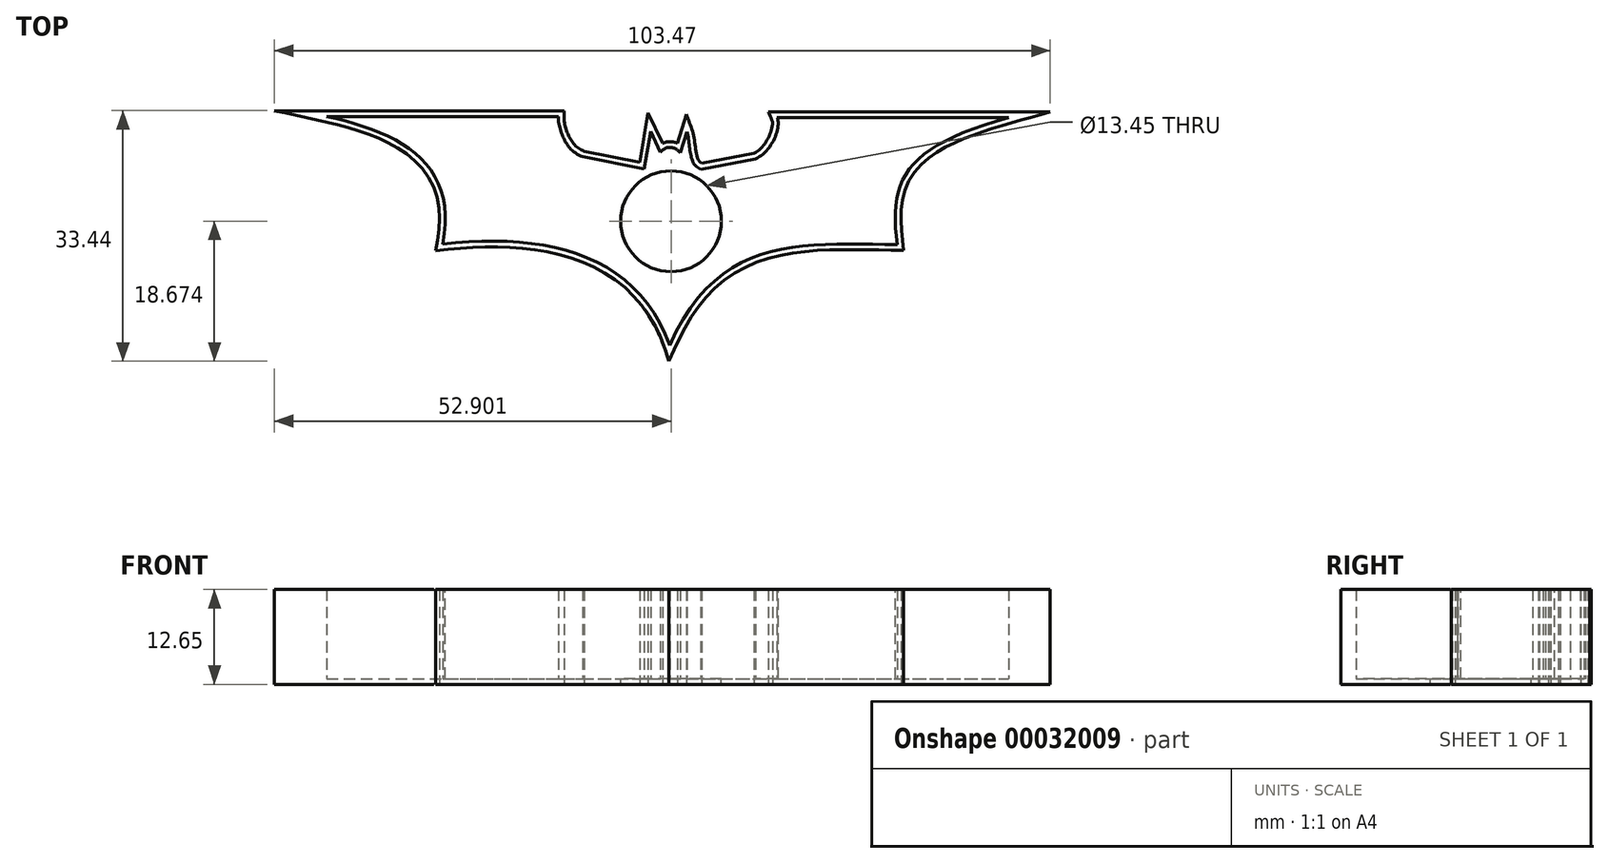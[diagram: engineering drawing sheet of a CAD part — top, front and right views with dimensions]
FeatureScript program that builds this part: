
annotation { "Feature Type Name" : "Feature", "Feature Type Description" : "" }
export const myFeature = defineFeature(function(context is Context, id is Id, definition is map)
    precondition{}
    {
        {
            var Q0;
            Q0=qCreatedBy(makeId("Top.planeOp"),FACE);
            var sketch = newSketch(context, id + "F0", { "sketchPlane" : qUnion([Q0])});
            skLineSegment(sketch, "E0", {"start": v(-52.23, 32.47) * mm, "end": v(-21.31, 32.47) * mm});
            skLineSegment(sketch, "E1", {"start": v(-21.31, 32.47) * mm, "end": v(-21.31, 31.76) * mm});
            skLineSegment(sketch, "E2", {"start": v(-18.1, 27.1) * mm, "end": v(-9.86, 25.43) * mm});
            skLineSegment(sketch, "E3", {"start": v(-9.02, 30.44) * mm, "end": v(-7.7, 27.7) * mm});
            skLineSegment(sketch, "E4", {"start": v(-2.32, 25.4) * mm, "end": v(4.99, 26.8) * mm});
            skLineSegment(sketch, "E5", {"start": v(7.87, 32.3) * mm, "end": v(38.75, 32.3) * mm});
            skLineSegment(sketch, "E6", {"start": v(-4.2, 30.42) * mm, "end": v(-5.06, 27.6) * mm});
            skFitSpline(sketch, "E7", {"points": [v(-52.23, 32.47) * mm, v(-36.75, 15.42) * mm], "startDerivative": vector(29.56, -6.55) * mm, "endDerivative": vector(-6.23, -32.56) * mm});
            skFitSpline(sketch, "E8", {"points": [v(-36.75, 15.42) * mm, v(-6.47, 1.88) * mm], "startDerivative": vector(40.4, 4.82) * mm, "endDerivative": vector(12.86, -36.98) * mm});
            skFitSpline(sketch, "E9", {"points": [v(-6.47, 1.88) * mm, v(23.88, 15.35) * mm], "startDerivative": vector(19.4, 44.22) * mm, "endDerivative": vector(38.19, -0.6) * mm});
            skFitSpline(sketch, "E10", {"points": [v(23.88, 15.35) * mm, v(38.75, 32.3) * mm], "startDerivative": vector(-3.42, 27.13) * mm, "endDerivative": vector(40.8, 11.46) * mm});
            skFitSpline(sketch, "E11", {"points": [v(7.87, 32.3) * mm, v(4.99, 26.8) * mm], "startDerivative": vector(1.8, -4.02) * mm, "endDerivative": vector(-6.23, -2.61) * mm});
            skFitSpline(sketch, "E12", {"points": [v(-2.32, 25.4) * mm, v(-4.2, 30.42) * mm], "startDerivative": vector(-5.43, 2.21) * mm, "endDerivative": vector(-1.88, 5.02) * mm});
            skFitSpline(sketch, "E13", {"points": [v(-5.06, 27.6) * mm, v(-7.7, 27.7) * mm], "startDerivative": vector(-2.61, 3.01) * mm, "endDerivative": vector(-2.3, -2.54) * mm});
            skFitSpline(sketch, "E14", {"points": [v(-9.86, 25.43) * mm, v(-9.02, 30.44) * mm], "startDerivative": vector(0.84, 5.01) * mm, "endDerivative": vector(0.84, 5.01) * mm});
            skFitSpline(sketch, "E15", {"points": [v(-21.31, 31.76) * mm, v(-18.1, 27.1) * mm], "startDerivative": vector(1.12, -5.61) * mm, "endDerivative": vector(6.13, -2.12) * mm});
            skSolve(sketch);
        }
        {
            var Q0;
            Q0=makeQuery(id+"F0.imprint","IMPRINT",FACE,{"disambiguationData":[TD([[makeQuery(id+"F0.imprint","IMPRINT",EDGE,{"derivedFrom":sQuery(id+"F0.wireOp",EDGE,"E0")}),-1.0]])]});
            extrude(context, id + "F1", {"entities" : qUnion([Q0]), "depth" : 11.9 * mm});
        }
        {
            var Q0;
            Q0=makeQuery(id+"F1.opExtrude","CAP_FACE",FACE,{"disambiguationData":[OSD([sQuery(id+"F0.wireOp",EDGE,"E0"),sQuery(id+"F0.wireOp",EDGE,"E1"),sQuery(id+"F0.wireOp",EDGE,"E2"),sQuery(id+"F0.wireOp",EDGE,"E3"),sQuery(id+"F0.wireOp",EDGE,"E4"),sQuery(id+"F0.wireOp",EDGE,"E5"),sQuery(id+"F0.wireOp",EDGE,"E6"),sQuery(id+"F0.wireOp",EDGE,"E7"),sQuery(id+"F0.wireOp",EDGE,"E8"),sQuery(id+"F0.wireOp",EDGE,"E9"),sQuery(id+"F0.wireOp",EDGE,"E10"),sQuery(id+"F0.wireOp",EDGE,"E11"),sQuery(id+"F0.wireOp",EDGE,"E12"),sQuery(id+"F0.wireOp",EDGE,"E13"),sQuery(id+"F0.wireOp",EDGE,"E14"),sQuery(id+"F0.wireOp",EDGE,"E15")])],"isStart":false});
            shell(context, id + "F2", {"entities" : qUnion([Q0]), "thickness" : 0.76 * mm, "oppositeDirection" : true});
        }
        {
            var Q0;
            Q0=makeQuery(id+"F2.opShell","OFFSET_FACE",FACE,{"disambiguationData":[OSD([sQuery(id+"F0.wireOp",EDGE,"E0"),sQuery(id+"F0.wireOp",EDGE,"E1"),sQuery(id+"F0.wireOp",EDGE,"E2"),sQuery(id+"F0.wireOp",EDGE,"E3"),sQuery(id+"F0.wireOp",EDGE,"E4"),sQuery(id+"F0.wireOp",EDGE,"E5"),sQuery(id+"F0.wireOp",EDGE,"E6"),sQuery(id+"F0.wireOp",EDGE,"E7"),sQuery(id+"F0.wireOp",EDGE,"E8"),sQuery(id+"F0.wireOp",EDGE,"E9"),sQuery(id+"F0.wireOp",EDGE,"E10"),sQuery(id+"F0.wireOp",EDGE,"E11"),sQuery(id+"F0.wireOp",EDGE,"E12"),sQuery(id+"F0.wireOp",EDGE,"E13"),sQuery(id+"F0.wireOp",EDGE,"E14"),sQuery(id+"F0.wireOp",EDGE,"E15")])]});
            var sketch = newSketch(context, id + "F3", { "sketchPlane" : qUnion([Q0])});
            skCircle(sketch, "E16", {"center": v(-6.29, 18.47) * mm, "radius": 6.72 * mm});
            skSolve(sketch);
        }
        {
            var Q0;
            Q0=makeQuery(id+"F3.imprint","IMPRINT",FACE,{"disambiguationData":[TD([[makeQuery(id+"F3.imprint","IMPRINT",EDGE,{"derivedFrom":sQuery(id+"F3.wireOp",EDGE,"E16")}),1.0]])]});
            extrude(context, id + "F4", {"entities" : qUnion([Q0]), "operationType" : NewBodyOperationType.REMOVE, "oppositeDirection" : true, "depth" : 25.4 * mm});
        }
    });
